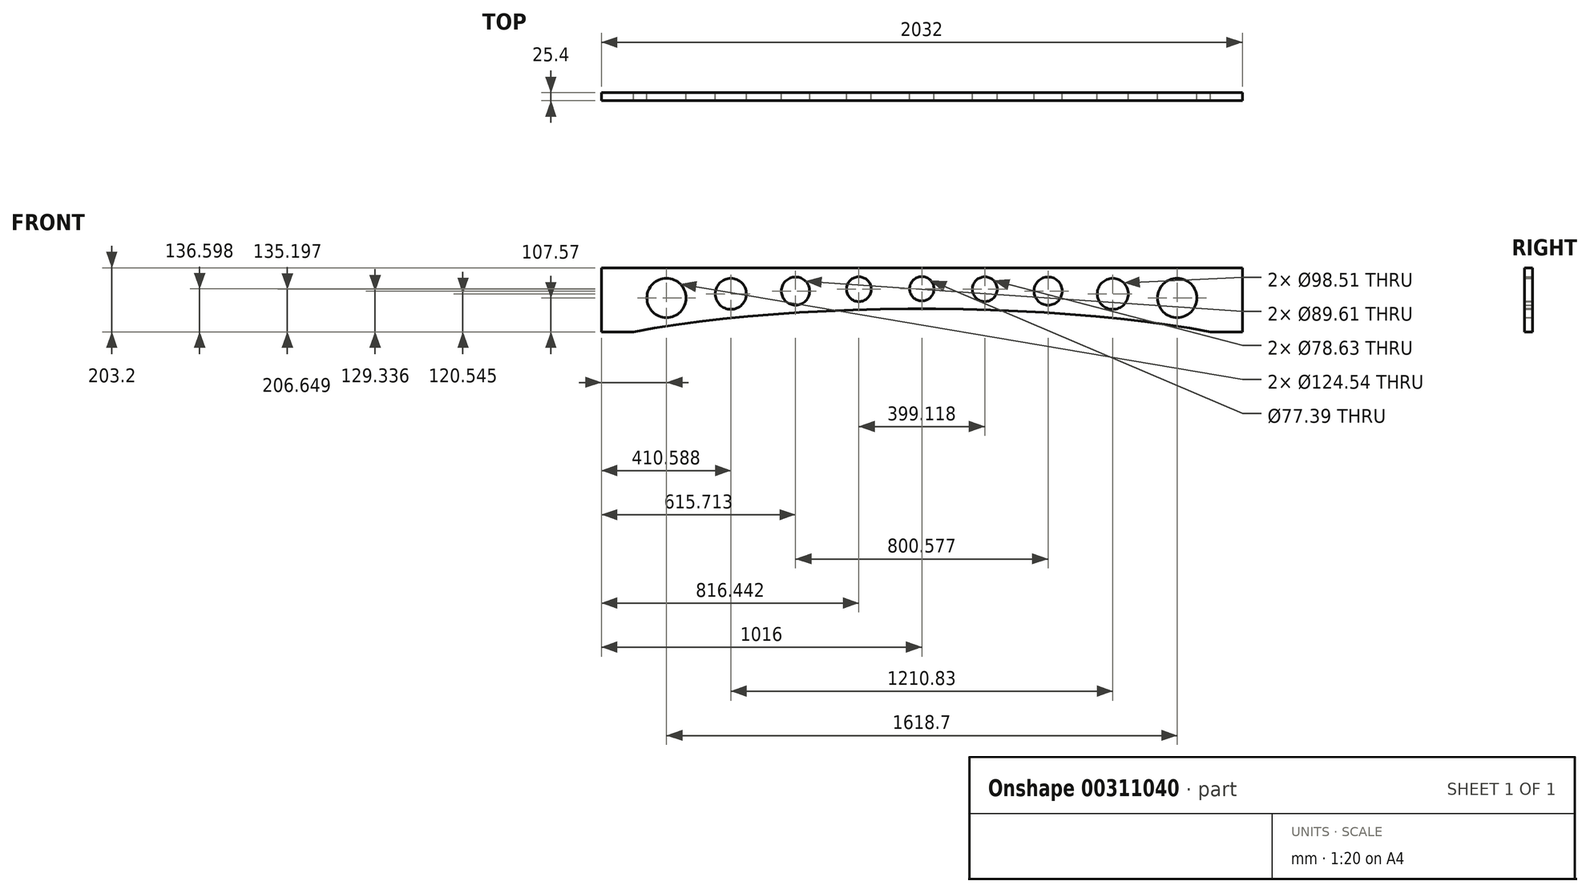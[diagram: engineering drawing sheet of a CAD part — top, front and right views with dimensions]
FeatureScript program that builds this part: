
annotation { "Feature Type Name" : "Feature", "Feature Type Description" : "" }
export const myFeature = defineFeature(function(context is Context, id is Id, definition is map)
    precondition{}
    {
        {
            var Q0;
            Q0=qCreatedBy(makeId("Front.planeOp"),FACE);
            var sketch = newSketch(context, id + "F0", { "sketchPlane" : qUnion([Q0])});
            skLineSegment(sketch, "E0.top", {"start": v(-124.94, 240.73) * mm, "end": v(1907.06, 240.73) * mm});
            skLineSegment(sketch, "E0.left", {"start": v(-124.94, 37.53) * mm, "end": v(-124.94, 240.73) * mm});
            skLineSegment(sketch, "E0.right", {"start": v(1907.06, 37.53) * mm, "end": v(1907.06, 240.73) * mm});
            skLineSegment(sketch, "E1", {"start": v(891.06, 240.73) * mm, "end": v(891.06, 122.87) * mm, "construction": true});
            skCircle(sketch, "E2", {"center": v(81.7, 145.1) * mm, "radius": 62.27 * mm});
            skLineSegment(sketch, "E3", {"start": v(-124.94, 37.53) * mm, "end": v(-23.34, 37.53) * mm});
            skLineSegment(sketch, "E4", {"start": v(1907.06, 37.53) * mm, "end": v(1805.46, 37.53) * mm});
            skEllipticalArc(sketch, "E5", {});
            skCircle(sketch, "E6", {"center": v(891.06, 174.13) * mm, "radius": 38.7 * mm});
            skCircle(sketch, "E7", {"center": v(490.77, 166.87) * mm, "radius": 44.8 * mm});
            skCircle(sketch, "E8", {"center": v(691.5, 172.73) * mm, "radius": 39.31 * mm});
            skCircle(sketch, "E9", {"center": v(285.65, 158.08) * mm, "radius": 49.25 * mm});
            skCircle(sketch, "E10.MirrorC", {"center": v(1090.62, 172.73) * mm, "radius": 39.31 * mm});
            skCircle(sketch, "E11.MirrorC", {"center": v(1291.35, 166.87) * mm, "radius": 44.8 * mm});
            skCircle(sketch, "E12.MirrorC", {"center": v(1496.47, 158.08) * mm, "radius": 49.25 * mm});
            skCircle(sketch, "E13.MirrorC", {"center": v(1700.41, 145.1) * mm, "radius": 62.27 * mm});
            const initialGuessF0  = {"E5": [0.8910610426068306, -0.16223667562007904, 1, 0, 1.3421538125872612, 0.2729062281249346, 0.8212687708496629, 2.32032388274013]};
            skSetInitialGuess(sketch, initialGuessF0);
            skSolve(sketch);
        }
        {
            var Q0;
            Q0=makeQuery(id+"F0.imprint","IMPRINT",FACE,{"disambiguationData":[TD([[makeQuery(id+"F0.imprint","IMPRINT",EDGE,{"derivedFrom":sQuery(id+"F0.wireOp",EDGE,"E0.top")}),-1.0]])]});
            extrude(context, id + "F1", {"entities" : qUnion([Q0]), "depth" : 25.4 * mm});
        }
    });
